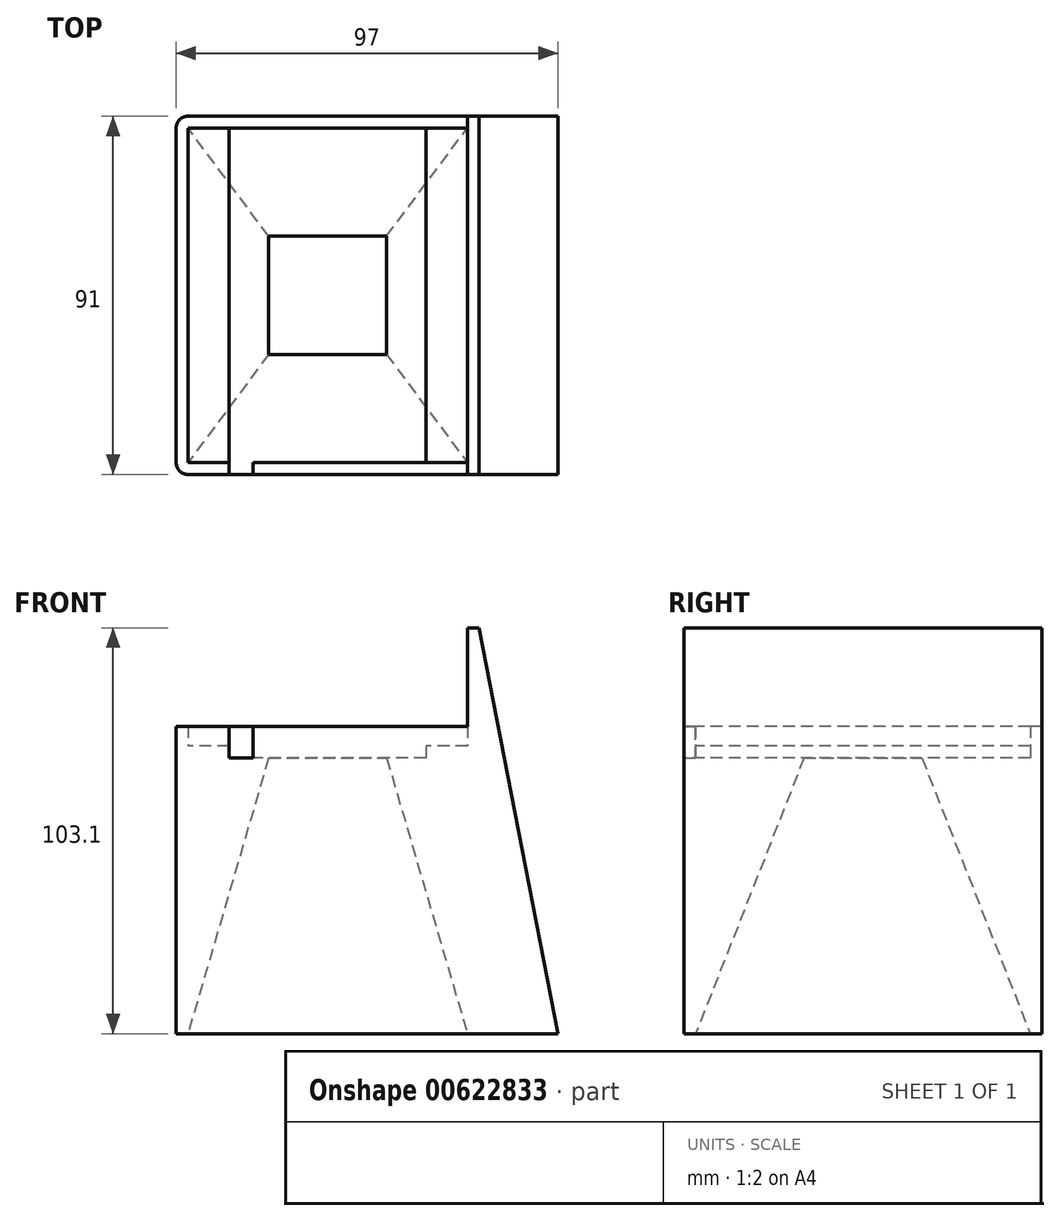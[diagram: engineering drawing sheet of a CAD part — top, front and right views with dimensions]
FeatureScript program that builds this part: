
annotation { "Feature Type Name" : "Feature", "Feature Type Description" : "" }
export const myFeature = defineFeature(function(context is Context, id is Id, definition is map)
    precondition{}
    {
        {
            var Q0;
            Q0=qCreatedBy(makeId("Top.planeOp"),FACE);
            var sketch = newSketch(context, id + "F0", { "sketchPlane" : qUnion([Q0])});
            skLineSegment(sketch, "E0.bottom", {"start": v(25, 42.5) * mm, "end": v(-25, 42.5) * mm});
            skLineSegment(sketch, "E0.top", {"start": v(25, -42.5) * mm, "end": v(-25, -42.5) * mm});
            skLineSegment(sketch, "E0.left", {"start": v(25, 42.5) * mm, "end": v(25, -42.5) * mm});
            skLineSegment(sketch, "E0.right", {"start": v(-25, 42.5) * mm, "end": v(-25, -42.5) * mm});
            skPoint(sketch, "E0.middle", {"position": v(0, 0) * mm});
            skLineSegment(sketch, "E1.bottom", {"start": v(38.5, 45.5) * mm, "end": v(-38.5, 45.5) * mm});
            skLineSegment(sketch, "E1.top", {"start": v(38.5, -45.5) * mm, "end": v(-38.5, -45.5) * mm});
            skLineSegment(sketch, "E1.left", {"start": v(38.5, 45.5) * mm, "end": v(38.5, -45.5) * mm});
            skLineSegment(sketch, "E1.right", {"start": v(-38.5, 45.5) * mm, "end": v(-38.5, -45.5) * mm});
            skSolve(sketch);
        }
        {
            var Q0;
            Q0 = qSketchRegion(id + "F0", true);
            extrude(context, id + "F1", {"entities" : qUnion([Q0]), "depth" : 3.1 * mm, "offsetDistance" : 25 * mm});
        }
        {
            var Q0;
            Q0=makeQuery(id+"F1.opExtrude","CAP_FACE",FACE,{"disambiguationData":[OSD([sQuery(id+"F0.wireOp",EDGE,"E0.bottom"),sQuery(id+"F0.wireOp",EDGE,"E0.top"),sQuery(id+"F0.wireOp",EDGE,"E0.left"),sQuery(id+"F0.wireOp",EDGE,"E0.right"),sQuery(id+"F0.wireOp",EDGE,"E1.bottom"),sQuery(id+"F0.wireOp",EDGE,"E1.top"),sQuery(id+"F0.wireOp",EDGE,"E1.left"),sQuery(id+"F0.wireOp",EDGE,"E1.right")])],"isStart":false});
            var sketch = newSketch(context, id + "F2", { "sketchPlane" : qUnion([Q0])});
            skLineSegment(sketch, "E2.bottom", {"start": v(35.5, 42.5) * mm, "end": v(-35.5, 42.5) * mm});
            skLineSegment(sketch, "E2.top", {"start": v(35.5, -42.5) * mm, "end": v(-35.5, -42.5) * mm});
            skLineSegment(sketch, "E2.left", {"start": v(35.5, 42.5) * mm, "end": v(35.5, -42.5) * mm});
            skLineSegment(sketch, "E2.right", {"start": v(-35.5, 42.5) * mm, "end": v(-35.5, -42.5) * mm});
            skPoint(sketch, "E2.middle", {"position": v(0, 0) * mm});
            skLineSegment(sketch, "E3.bottom", {"start": v(38.5, 45.5) * mm, "end": v(-38.5, 45.5) * mm});
            skLineSegment(sketch, "E3.top", {"start": v(38.5, -45.5) * mm, "end": v(-38.5, -45.5) * mm});
            skLineSegment(sketch, "E3.left", {"start": v(38.5, 45.5) * mm, "end": v(38.5, -45.5) * mm});
            skLineSegment(sketch, "E3.right", {"start": v(-38.5, 45.5) * mm, "end": v(-38.5, -45.5) * mm});
            skSolve(sketch);
        }
        {
            var Q0;
            Q0 = qSketchRegion(id + "F2", true);
            extrude(context, id + "F3", {"entities" : qUnion([Q0]), "operationType" : NewBodyOperationType.ADD, "depth" : 5 * mm, "offsetDistance" : 25 * mm});
        }
        {
            var Q0;
            Q0=makeQuery(id+"F3.opExtrude","CAP_FACE",FACE,{"disambiguationData":[OSD([sQuery(id+"F2.wireOp",EDGE,"E2.bottom"),sQuery(id+"F2.wireOp",EDGE,"E2.top"),sQuery(id+"F2.wireOp",EDGE,"E2.left"),sQuery(id+"F2.wireOp",EDGE,"E2.right"),sQuery(id+"F2.wireOp",EDGE,"E3.bottom"),sQuery(id+"F2.wireOp",EDGE,"E3.top"),sQuery(id+"F2.wireOp",EDGE,"E3.left"),sQuery(id+"F2.wireOp",EDGE,"E3.right")])],"isStart":false});
            var sketch = newSketch(context, id + "F4", { "sketchPlane" : qUnion([Q0])});
            skLineSegment(sketch, "E4.bottom", {"start": v(-38.5, 45.5) * mm, "end": v(-35.5, 45.5) * mm});
            skLineSegment(sketch, "E4.top", {"start": v(-38.5, -45.5) * mm, "end": v(-35.5, -45.5) * mm});
            skLineSegment(sketch, "E4.left", {"start": v(-38.5, 45.5) * mm, "end": v(-38.5, -45.5) * mm});
            skLineSegment(sketch, "E4.right", {"start": v(-35.5, 45.5) * mm, "end": v(-35.5, -45.5) * mm});
            skLineSegment(sketch, "E5.bottom", {"start": v(38.5, 45.5) * mm, "end": v(35.5, 45.5) * mm});
            skLineSegment(sketch, "E5.top", {"start": v(38.5, -45.5) * mm, "end": v(35.5, -45.5) * mm});
            skLineSegment(sketch, "E5.left", {"start": v(38.5, 45.5) * mm, "end": v(38.5, -45.5) * mm});
            skLineSegment(sketch, "E5.right", {"start": v(35.5, 45.5) * mm, "end": v(35.5, -45.5) * mm});
            skSolve(sketch);
        }
        {
            var Q0;
            Q0 = qSketchRegion(id + "F4", true);
            extrude(context, id + "F5", {"entities" : qUnion([Q0]), "operationType" : NewBodyOperationType.ADD, "depth" : 25 * mm, "offsetDistance" : 25 * mm});
        }
        {
            var Q0;
            Q0=makeQuery(id+"F1.opExtrude","CAP_FACE",FACE,{"disambiguationData":[OSD([sQuery(id+"F0.wireOp",EDGE,"E0.bottom"),sQuery(id+"F0.wireOp",EDGE,"E0.top"),sQuery(id+"F0.wireOp",EDGE,"E0.left"),sQuery(id+"F0.wireOp",EDGE,"E0.right"),sQuery(id+"F0.wireOp",EDGE,"E1.bottom"),sQuery(id+"F0.wireOp",EDGE,"E1.top"),sQuery(id+"F0.wireOp",EDGE,"E1.left"),sQuery(id+"F0.wireOp",EDGE,"E1.right")])],"isStart":true});
            var sketch = newSketch(context, id + "F6", { "sketchPlane" : qUnion([Q0])});
            skLineSegment(sketch, "E6.bottom", {"start": v(38.5, 45.5) * mm, "end": v(-38.5, 45.5) * mm});
            skLineSegment(sketch, "E6.top", {"start": v(38.5, -45.5) * mm, "end": v(-38.5, -45.5) * mm});
            skLineSegment(sketch, "E6.left", {"start": v(38.5, 45.5) * mm, "end": v(38.5, -45.5) * mm});
            skLineSegment(sketch, "E6.right", {"start": v(-38.5, 45.5) * mm, "end": v(-38.5, -45.5) * mm});
            skPoint(sketch, "E6.middle", {"position": v(0, 0) * mm});
            skLineSegment(sketch, "E7.bottom", {"start": v(35.5, 42.5) * mm, "end": v(-35.5, 42.5) * mm});
            skLineSegment(sketch, "E7.top", {"start": v(35.5, -42.5) * mm, "end": v(-35.5, -42.5) * mm});
            skLineSegment(sketch, "E7.left", {"start": v(35.5, 42.5) * mm, "end": v(35.5, -42.5) * mm});
            skLineSegment(sketch, "E7.right", {"start": v(-35.5, 42.5) * mm, "end": v(-35.5, -42.5) * mm});
            skLineSegment(sketch, "E8.bottom", {"start": v(15, 15) * mm, "end": v(-15, 15) * mm, "construction": true});
            skLineSegment(sketch, "E8.top", {"start": v(15, -15) * mm, "end": v(-15, -15) * mm, "construction": true});
            skLineSegment(sketch, "E8.left", {"start": v(15, 15) * mm, "end": v(15, -15) * mm, "construction": true});
            skLineSegment(sketch, "E8.right", {"start": v(-15, 15) * mm, "end": v(-15, -15) * mm, "construction": true});
            skSolve(sketch);
        }
        {
            var Q0;
            Q0 = qSketchRegion(id + "F6", true);
            extrude(context, id + "F7", {"entities" : qUnion([Q0]), "operationType" : NewBodyOperationType.ADD, "depth" : 70 * mm, "offsetDistance" : 25 * mm});
        }
        {
            var Q0;
            Q0=makeQuery(id+"F7.boolean.opBoolean","MERGE",FACE,{"derivedFrom":[makeQuery(id+"F5.boolean.opBoolean","MERGE",FACE,{"derivedFrom":[makeQuery(id+"F3.boolean.opBoolean","MERGE",FACE,{"derivedFrom":[makeQuery(id+"F1.opExtrude","SWEPT_FACE",FACE,{"disambiguationData":[OSD([sQuery(id+"F0.wireOp",EDGE,"E1.bottom")])]}),makeQuery(id+"F3.opExtrude","SWEPT_FACE",FACE,{"disambiguationData":[OSD([sQuery(id+"F2.wireOp",EDGE,"E3.bottom")])]})]}),makeQuery(id+"F5.opExtrude","SWEPT_FACE",FACE,{"disambiguationData":[OSD([sQuery(id+"F4.wireOp",EDGE,"E4.bottom")])]}),makeQuery(id+"F5.opExtrude","SWEPT_FACE",FACE,{"disambiguationData":[OSD([sQuery(id+"F4.wireOp",EDGE,"E5.bottom")])]})]}),makeQuery(id+"F7.opExtrude","SWEPT_FACE",FACE,{"disambiguationData":[OSD([sQuery(id+"F6.wireOp",EDGE,"E6.top")])]})]});
            var sketch = newSketch(context, id + "F8", { "sketchPlane" : qUnion([Q0])});
            skLineSegment(sketch, "E9", {"start": v(38.5, 0) * mm, "end": v(15, 0) * mm});
            skLineSegment(sketch, "E10", {"start": v(38.5, 0) * mm, "end": v(38.5, -70) * mm});
            skLineSegment(sketch, "E11", {"start": v(38.5, -70) * mm, "end": v(35.5, -70) * mm});
            skLineSegment(sketch, "E12", {"start": v(35.5, -70) * mm, "end": v(15, 0) * mm});
            skLineSegment(sketch, "E13", {"start": v(-38.5, 0) * mm, "end": v(-15, 0) * mm});
            skLineSegment(sketch, "E14", {"start": v(-38.5, 0) * mm, "end": v(-38.5, -70) * mm});
            skLineSegment(sketch, "E15", {"start": v(-38.5, -70) * mm, "end": v(-35.5, -70) * mm});
            skLineSegment(sketch, "E16", {"start": v(-35.5, -70) * mm, "end": v(-15, 0) * mm});
            skSolve(sketch);
        }
        {
            var Q0;
            Q0 = qSketchRegion(id + "F8", true);
            extrude(context, id + "F9", {"entities" : qUnion([Q0]), "operationType" : NewBodyOperationType.ADD, "oppositeDirection" : true, "depth" : 91 * mm, "offsetDistance" : 25 * mm});
        }
        {
            var Q0;
            Q0=makeQuery(id+"F7.boolean.opBoolean","MERGE",FACE,{"derivedFrom":[makeQuery(id+"F5.boolean.opBoolean","MERGE",FACE,{"derivedFrom":[makeQuery(id+"F3.boolean.opBoolean","MERGE",FACE,{"derivedFrom":[makeQuery(id+"F1.opExtrude","SWEPT_FACE",FACE,{"disambiguationData":[OSD([sQuery(id+"F0.wireOp",EDGE,"E1.left")])]}),makeQuery(id+"F3.opExtrude","SWEPT_FACE",FACE,{"disambiguationData":[OSD([sQuery(id+"F2.wireOp",EDGE,"E3.left")])]})]}),makeQuery(id+"F5.opExtrude","SWEPT_FACE",FACE,{"disambiguationData":[OSD([sQuery(id+"F4.wireOp",EDGE,"E5.left")])]})]}),makeQuery(id+"F7.opExtrude","SWEPT_FACE",FACE,{"disambiguationData":[OSD([sQuery(id+"F6.wireOp",EDGE,"E6.left")])]})]});
            var sketch = newSketch(context, id + "F10", { "sketchPlane" : qUnion([Q0])});
            skLineSegment(sketch, "E17", {"start": v(45.5, 0) * mm, "end": v(15, 0) * mm});
            skLineSegment(sketch, "E18", {"start": v(45.5, 0) * mm, "end": v(45.5, -70) * mm});
            skLineSegment(sketch, "E19", {"start": v(45.5, -70) * mm, "end": v(42.5, -70) * mm});
            skLineSegment(sketch, "E20", {"start": v(42.5, -70) * mm, "end": v(15, 0) * mm});
            skLineSegment(sketch, "E21", {"start": v(-45.5, 0) * mm, "end": v(-15, 0) * mm});
            skLineSegment(sketch, "E22", {"start": v(-45.5, 0) * mm, "end": v(-45.5, -70) * mm});
            skLineSegment(sketch, "E23", {"start": v(-45.5, -70) * mm, "end": v(-42.5, -70) * mm});
            skLineSegment(sketch, "E24", {"start": v(-42.5, -70) * mm, "end": v(-15, 0) * mm});
            skSolve(sketch);
        }
        {
            var Q0;
            Q0 = qSketchRegion(id + "F10", true);
            extrude(context, id + "F11", {"entities" : qUnion([Q0]), "operationType" : NewBodyOperationType.ADD, "oppositeDirection" : true, "depth" : 77 * mm, "offsetDistance" : 25 * mm});
        }
        {
            var Q0;
            Q0=makeQuery(id+"F7.boolean.opBoolean","MERGE",FACE,{"derivedFrom":[makeQuery(id+"F3.boolean.opBoolean","MERGE",FACE,{"derivedFrom":[makeQuery(id+"F1.opExtrude","SWEPT_FACE",FACE,{"disambiguationData":[OSD([sQuery(id+"F0.wireOp",EDGE,"E0.top")])]}),makeQuery(id+"F3.opExtrude","SWEPT_FACE",FACE,{"disambiguationData":[OSD([sQuery(id+"F2.wireOp",EDGE,"E2.top")])]})]}),makeQuery(id+"F7.opExtrude","SWEPT_FACE",FACE,{"disambiguationData":[OSD([sQuery(id+"F6.wireOp",EDGE,"E7.bottom")])]})]});
            var sketch = newSketch(context, id + "F12", { "sketchPlane" : qUnion([Q0])});
            skLineSegment(sketch, "E25.bottom", {"start": v(25, 0) * mm, "end": v(19, 0) * mm});
            skLineSegment(sketch, "E25.top", {"start": v(25, 8.1) * mm, "end": v(19, 8.1) * mm});
            skLineSegment(sketch, "E25.left", {"start": v(25, 0) * mm, "end": v(25, 8.1) * mm});
            skLineSegment(sketch, "E25.right", {"start": v(19, 0) * mm, "end": v(19, 8.1) * mm});
            skSolve(sketch);
        }
        {
            var Q0;
            Q0 = qSketchRegion(id + "F12", true);
            extrude(context, id + "F13", {"entities" : qUnion([Q0]), "operationType" : NewBodyOperationType.REMOVE, "oppositeDirection" : true, "depth" : 4 * mm, "offsetDistance" : 25 * mm});
        }
        {
            var Q0;
            Q0=makeQuery(id+"F7.boolean.opBoolean","MERGE",FACE,{"derivedFrom":[makeQuery(id+"F5.boolean.opBoolean","MERGE",FACE,{"derivedFrom":[makeQuery(id+"F3.boolean.opBoolean","MERGE",FACE,{"derivedFrom":[makeQuery(id+"F1.opExtrude","SWEPT_FACE",FACE,{"disambiguationData":[OSD([sQuery(id+"F0.wireOp",EDGE,"E1.top")])]}),makeQuery(id+"F3.opExtrude","SWEPT_FACE",FACE,{"disambiguationData":[OSD([sQuery(id+"F2.wireOp",EDGE,"E3.top")])]})]}),makeQuery(id+"F5.opExtrude","SWEPT_FACE",FACE,{"disambiguationData":[OSD([sQuery(id+"F4.wireOp",EDGE,"E4.top")])]}),makeQuery(id+"F5.opExtrude","SWEPT_FACE",FACE,{"disambiguationData":[OSD([sQuery(id+"F4.wireOp",EDGE,"E5.top")])]})]}),makeQuery(id+"F7.opExtrude","SWEPT_FACE",FACE,{"disambiguationData":[OSD([sQuery(id+"F6.wireOp",EDGE,"E6.bottom")])]})]});
            var sketch = newSketch(context, id + "F14", { "sketchPlane" : qUnion([Q0])});
            skLineSegment(sketch, "E26", {"start": v(38.5, 33.1) * mm, "end": v(38.5, -70) * mm});
            skLineSegment(sketch, "E27", {"start": v(38.5, -70) * mm, "end": v(58.5, -70) * mm});
            skLineSegment(sketch, "E28", {"start": v(58.5, -70) * mm, "end": v(38.5, 33.1) * mm});
            skSolve(sketch);
        }
        {
            var Q0;
            Q0 = qSketchRegion(id + "F14", true);
            extrude(context, id + "F15", {"entities" : qUnion([Q0]), "operationType" : NewBodyOperationType.ADD, "oppositeDirection" : true, "depth" : 91 * mm, "offsetDistance" : 25 * mm});
        }
        {
            var Q0;
            Q0=makeQuery(id+"F5.opExtrude","CAP_FACE",FACE,{"disambiguationData":[OSD([sQuery(id+"F4.wireOp",EDGE,"E4.bottom"),sQuery(id+"F4.wireOp",EDGE,"E4.top"),sQuery(id+"F4.wireOp",EDGE,"E4.left"),sQuery(id+"F4.wireOp",EDGE,"E4.right")])],"isStart":false});
            var sketch = newSketch(context, id + "F16", { "sketchPlane" : qUnion([Q0])});
            skLineSegment(sketch, "E29.bottom", {"start": v(-38.5, 45.5) * mm, "end": v(-35.5, 45.5) * mm});
            skLineSegment(sketch, "E29.top", {"start": v(-38.5, -45.5) * mm, "end": v(-35.5, -45.5) * mm});
            skLineSegment(sketch, "E29.left", {"start": v(-38.5, 45.5) * mm, "end": v(-38.5, -45.5) * mm});
            skLineSegment(sketch, "E29.right", {"start": v(-35.5, 45.5) * mm, "end": v(-35.5, -45.5) * mm});
            skSolve(sketch);
        }
        {
            var Q0;
            Q0 = qSketchRegion(id + "F16", true);
            extrude(context, id + "F17", {"entities" : qUnion([Q0]), "operationType" : NewBodyOperationType.REMOVE, "oppositeDirection" : true, "depth" : 25 * mm, "offsetDistance" : 25 * mm});
        }
        {
            var Q0;
            Q0=makeQuery(id+"F7.boolean.opBoolean","MERGE",EDGE,{"derivedFrom":[makeQuery(id+"F5.boolean.opBoolean","MERGE",EDGE,{"derivedFrom":[makeQuery(id+"F3.boolean.opBoolean","MERGE",EDGE,{"derivedFrom":[makeQuery(id+"F1.opExtrude","SWEPT_EDGE",EDGE,{"disambiguationData":[OSD([sQuery(id+"F0.wireOp",EDGE,"E1.top"),sQuery(id+"F0.wireOp",EDGE,"E1.right")])]}),makeQuery(id+"F3.opExtrude","SWEPT_EDGE",EDGE,{"disambiguationData":[OSD([sQuery(id+"F2.wireOp",EDGE,"E3.top"),sQuery(id+"F2.wireOp",EDGE,"E3.right")])]})]}),makeQuery(id+"F5.opExtrude","SWEPT_EDGE",EDGE,{"disambiguationData":[OSD([sQuery(id+"F4.wireOp",EDGE,"E4.top"),sQuery(id+"F4.wireOp",EDGE,"E4.left")])]})]}),makeQuery(id+"F7.opExtrude","SWEPT_EDGE",EDGE,{"disambiguationData":[OSD([sQuery(id+"F6.wireOp",EDGE,"E6.bottom"),sQuery(id+"F6.wireOp",EDGE,"E6.right")])]})]});
            var Q1;
            Q1=makeQuery(id+"F7.boolean.opBoolean","MERGE",EDGE,{"derivedFrom":[makeQuery(id+"F5.boolean.opBoolean","MERGE",EDGE,{"derivedFrom":[makeQuery(id+"F3.boolean.opBoolean","MERGE",EDGE,{"derivedFrom":[makeQuery(id+"F1.opExtrude","SWEPT_EDGE",EDGE,{"disambiguationData":[OSD([sQuery(id+"F0.wireOp",EDGE,"E1.bottom"),sQuery(id+"F0.wireOp",EDGE,"E1.right")])]}),makeQuery(id+"F3.opExtrude","SWEPT_EDGE",EDGE,{"disambiguationData":[OSD([sQuery(id+"F2.wireOp",EDGE,"E3.bottom"),sQuery(id+"F2.wireOp",EDGE,"E3.right")])]})]}),makeQuery(id+"F5.opExtrude","SWEPT_EDGE",EDGE,{"disambiguationData":[OSD([sQuery(id+"F4.wireOp",EDGE,"E4.bottom"),sQuery(id+"F4.wireOp",EDGE,"E4.left")])]})]}),makeQuery(id+"F7.opExtrude","SWEPT_EDGE",EDGE,{"disambiguationData":[OSD([sQuery(id+"F6.wireOp",EDGE,"E6.top"),sQuery(id+"F6.wireOp",EDGE,"E6.right")])]})]});
            fillet(context, id + "F18", {"entities" : qUnion([Q0, Q1]), "tangentPropagation" : true, "radius" : 3 * mm, "defaultsChanged" : false, "vertexSettings" : [], "allowEdgeOverflow" : false});
        }
    });
